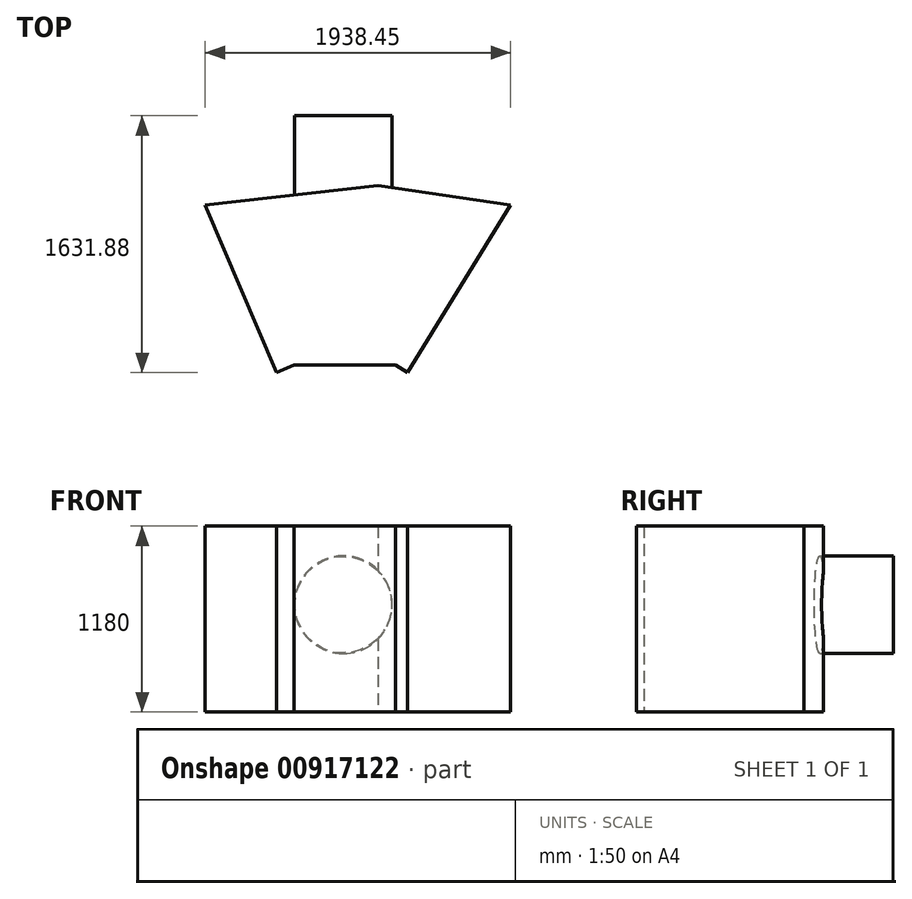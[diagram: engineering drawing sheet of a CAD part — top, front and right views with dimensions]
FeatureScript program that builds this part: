
annotation { "Feature Type Name" : "Feature", "Feature Type Description" : "" }
export const myFeature = defineFeature(function(context is Context, id is Id, definition is map)
    precondition{}
    {
        {
            var Q0;
            Q0=qCreatedBy(makeId("Front.planeOp"),FACE);
            var sketch = newSketch(context, id + "F0", { "sketchPlane" : qUnion([Q0])});
            skLineSegment(sketch, "E0.bottom", {"start": v(-1605.4, 0) * mm, "end": v(-4579.46, 0) * mm});
            skLineSegment(sketch, "E0.top", {"start": v(-1605.4, -759) * mm, "end": v(-4579.46, -759) * mm});
            skLineSegment(sketch, "E0.left", {"start": v(-1605.4, 0) * mm, "end": v(-1605.4, -759) * mm});
            skLineSegment(sketch, "E0.right", {"start": v(-4579.46, 0) * mm, "end": v(-4579.46, -759) * mm});
            skLineSegment(sketch, "E1", {"start": v(-1605.4, 0) * mm, "end": v(-1605.4, 0) * mm});
            skLineSegment(sketch, "E2", {"start": v(-1605.4, -759) * mm, "end": v(-1605.4, 0) * mm});
            skLineSegment(sketch, "E3", {"start": v(-1605.4, -759) * mm, "end": v(-1605.4, -759) * mm});
            skCircle(sketch, "E4", {"center": v(-2880, 680.54) * mm, "radius": 310.05 * mm});
            skSolve(sketch);
        }
        {
            var Q0;
            Q0=makeQuery(id+"F0.imprint","IMPRINT",FACE,{"disambiguationData":[TD([[makeQuery(id+"F0.imprint","IMPRINT",EDGE,{"derivedFrom":sQuery(id+"F0.wireOp",EDGE,"E4")}),1.0]])]});
            extrude(context, id + "F1", {"entities" : qUnion([Q0]), "depth" : 70 * mm, "offsetDistance" : 25 * mm});
        }
        {
            var Q0;
            Q0=makeQuery(id+"F1.opExtrude","CAP_FACE",FACE,{"disambiguationData":[OSD([sQuery(id+"F0.wireOp",EDGE,"E4")])],"isStart":false});
            var Q1;
            Q1=makeQuery(id+"F1.opExtrude","CAP_FACE",FACE,{"disambiguationData":[OSD([sQuery(id+"F0.wireOp",EDGE,"E4")])],"isStart":true});
            extrude(context, id + "F2", {"entities" : qUnion([Q0, Q1]), "operationType" : NewBodyOperationType.ADD, "depth" : 800 * mm, "offsetDistance" : 25 * mm});
        }
        {
            var Q0;
            Q0=qCreatedBy(makeId("Top.planeOp"),FACE);
            var sketch = newSketch(context, id + "F3", { "sketchPlane" : qUnion([Q0])});
            skLineSegment(sketch, "E5", {"start": v(-3304.87, -1631.88) * mm, "end": v(-3756.29, -567.88) * mm});
            skLineSegment(sketch, "E6", {"start": v(-3304.87, -1631.88) * mm, "end": v(-3193.85, -1584.78) * mm});
            skLineSegment(sketch, "E7", {"start": v(-2472.84, -1631.88) * mm, "end": v(-1817.84, -567.88) * mm});
            skLineSegment(sketch, "E8", {"start": v(-2472.84, -1631.88) * mm, "end": v(-2549.35, -1584.78) * mm});
            skLineSegment(sketch, "E9", {"start": v(-1817.84, -567.88) * mm, "end": v(-2658.72, -442.7) * mm});
            skLineSegment(sketch, "E10", {"start": v(-3756.29, -567.88) * mm, "end": v(-2658.72, -442.7) * mm});
            skLineSegment(sketch, "E11", {"start": v(-3193.85, -1584.78) * mm, "end": v(-2549.35, -1584.78) * mm});
            skSolve(sketch);
        }
        {
            var Q0;
            Q0 = qSketchRegion(id + "F3", true);
            extrude(context, id + "F4", {"entities" : qUnion([Q0]), "operationType" : NewBodyOperationType.ADD, "depth" : 1180 * mm, "offsetDistance" : 25 * mm});
        }
    });
